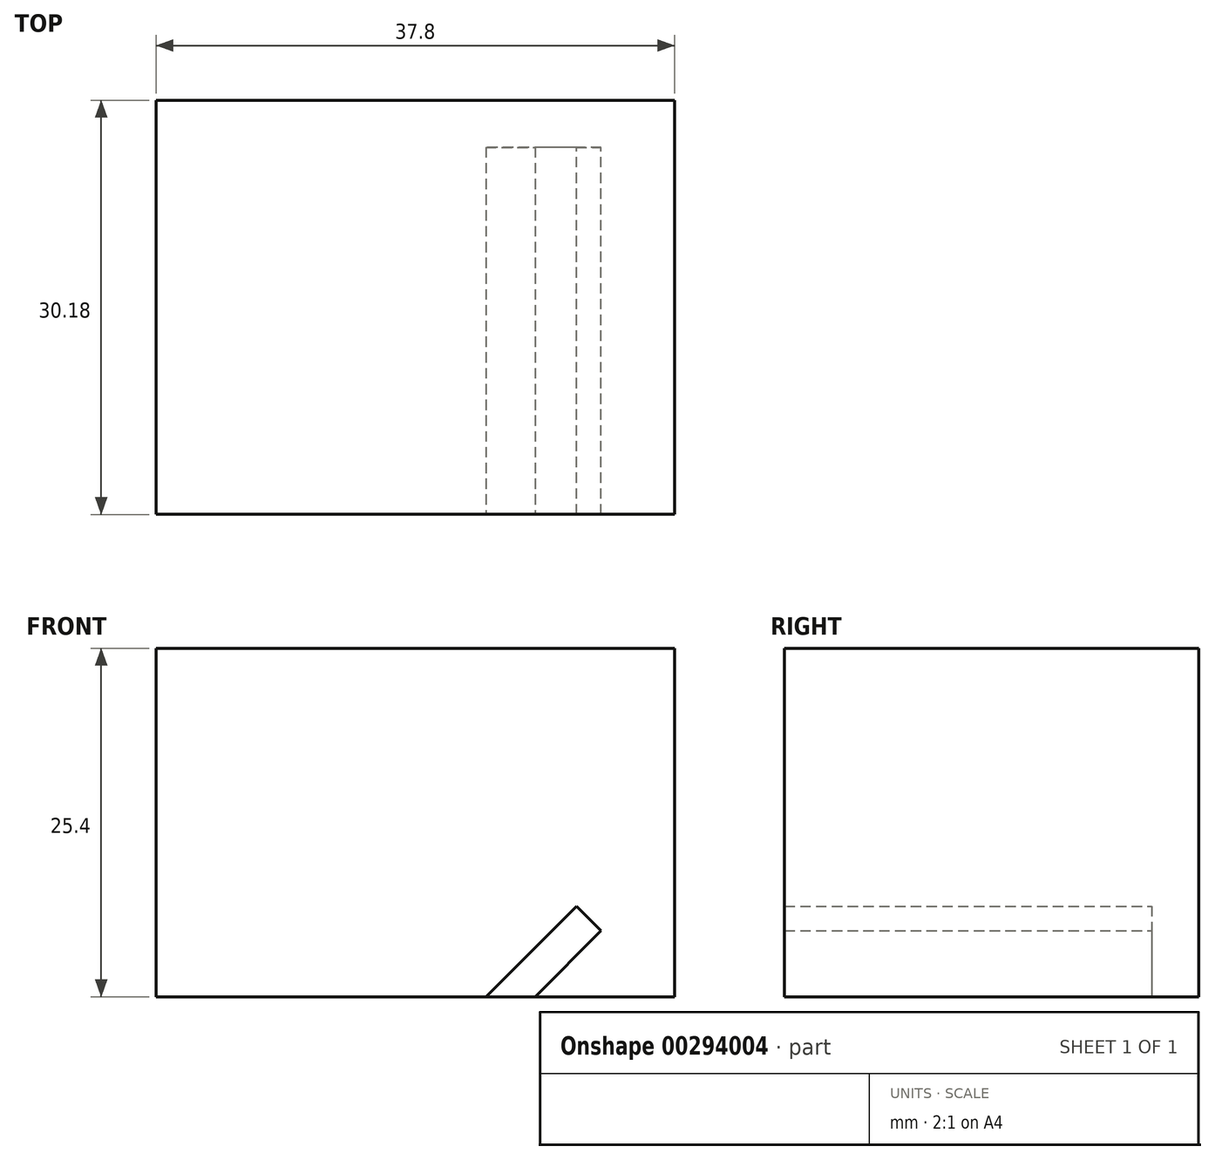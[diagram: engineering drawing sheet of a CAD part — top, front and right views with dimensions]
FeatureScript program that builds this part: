
annotation { "Feature Type Name" : "Feature", "Feature Type Description" : "" }
export const myFeature = defineFeature(function(context is Context, id is Id, definition is map)
    precondition{}
    {
        {
            var Q0;
            Q0=qCreatedBy(makeId("Top.planeOp"),FACE);
            var sketch = newSketch(context, id + "F0", { "sketchPlane" : qUnion([Q0])});
            skLineSegment(sketch, "E0.bottom", {"start": v(-18.9, 15.09) * mm, "end": v(18.9, 15.09) * mm});
            skLineSegment(sketch, "E0.top", {"start": v(-18.9, -15.09) * mm, "end": v(18.9, -15.09) * mm});
            skLineSegment(sketch, "E0.left", {"start": v(-18.9, 15.09) * mm, "end": v(-18.9, -15.09) * mm});
            skLineSegment(sketch, "E0.right", {"start": v(18.9, 15.09) * mm, "end": v(18.9, -15.09) * mm});
            skPoint(sketch, "E0.middle", {"position": v(0, 0) * mm});
            skSolve(sketch);
        }
        {
            var Q0;
            Q0=makeQuery(id+"F0.imprint","IMPRINT",FACE,{"disambiguationData":[TD([[makeQuery(id+"F0.imprint","IMPRINT",EDGE,{"derivedFrom":sQuery(id+"F0.wireOp",EDGE,"E0.bottom")}),-1.0]])]});
            extrude(context, id + "F1", {"entities" : qUnion([Q0]), "depth" : 25.4 * mm});
        }
        {
            var Q0;
            Q0=qCreatedBy(makeId("Top.planeOp"),FACE);
            var sketch = newSketch(context, id + "F2", { "sketchPlane" : qUnion([Q0])});
            skLineSegment(sketch, "E1", {"start": v(28.26, 33.6) * mm, "end": v(28.26, -37.05) * mm});
            skSolve(sketch);
        }
        {
            var Q0;
            Q0=sQuery(id+"F2.wireOp",EDGE,"E1");
            cPlane(context, id + "F3", {"entities" : qUnion([Q0]), "cplaneType" : CPlaneType.LINE_ANGLE, "offset" : 25.4 * mm, "angle" : 225 * degree, "width" : 152.4 * mm, "height" : 152.4 * mm});
        }
        {
            var Q0;
            Q0=qCreatedBy(id+"F3.planeOp",FACE);
            var sketch = newSketch(context, id + "F4", { "sketchPlane" : qUnion([Q0])});
            skLineSegment(sketch, "E2.bottom", {"start": v(32.05, 26.78) * mm, "end": v(-11.67, 26.78) * mm});
            skLineSegment(sketch, "E2.top", {"start": v(32.05, -93.26) * mm, "end": v(-11.67, -93.26) * mm});
            skLineSegment(sketch, "E2.left", {"start": v(32.05, 26.78) * mm, "end": v(32.05, -93.26) * mm});
            skLineSegment(sketch, "E2.right", {"start": v(-11.67, 26.78) * mm, "end": v(-11.67, -93.26) * mm});
            skPoint(sketch, "E2.middle", {"position": v(10.19, -33.24) * mm});
            skSolve(sketch);
        }
        {
            var Q0;
            Q0=makeQuery(id+"F4.imprint","IMPRINT",FACE,{"disambiguationData":[TD([[makeQuery(id+"F4.imprint","IMPRINT",EDGE,{"derivedFrom":sQuery(id+"F4.wireOp",EDGE,"E2.bottom")}),1.0]])]});
            extrude(context, id + "F5", {"entities" : qUnion([Q0]), "depth" : 2.54 * mm});
        }
        {
            var Q0;
            Q0=makeQuery(id+"F5.opExtrude","SWEPT_BODY",BODY,{"disambiguationData":[OSD([sQuery(id+"F4.wireOp",EDGE,"E2.bottom"),sQuery(id+"F4.wireOp",EDGE,"E2.top"),sQuery(id+"F4.wireOp",EDGE,"E2.left"),sQuery(id+"F4.wireOp",EDGE,"E2.right")])]});
            transform(context, id + "F6", {"entities" : qUnion([Q0]), "transformType" : TransformType.TRANSLATION_3D, "dx" : -19.53 * mm, "dy" : 0 * mm, "dz" : 0 * mm, "makeCopy" : false});
        }
        {
            var Q0;
            Q0=makeQuery(id+"F5.opExtrude","SWEPT_BODY",BODY,{"disambiguationData":[OSD([sQuery(id+"F4.wireOp",EDGE,"E2.bottom"),sQuery(id+"F4.wireOp",EDGE,"E2.top"),sQuery(id+"F4.wireOp",EDGE,"E2.left"),sQuery(id+"F4.wireOp",EDGE,"E2.right")])]});
            var Q1;
            Q1=makeQuery(id+"F1.opExtrude","SWEPT_BODY",BODY,{"disambiguationData":[OSD([sQuery(id+"F0.wireOp",EDGE,"E0.bottom"),sQuery(id+"F0.wireOp",EDGE,"E0.top"),sQuery(id+"F0.wireOp",EDGE,"E0.left"),sQuery(id+"F0.wireOp",EDGE,"E0.right")])]});
            booleanBodies(context, id + "F7", {"operationType" : BooleanOperationType.SUBTRACTION, "tools" : qUnion([Q0]), "targets" : qUnion([Q1])});
        }
    });
